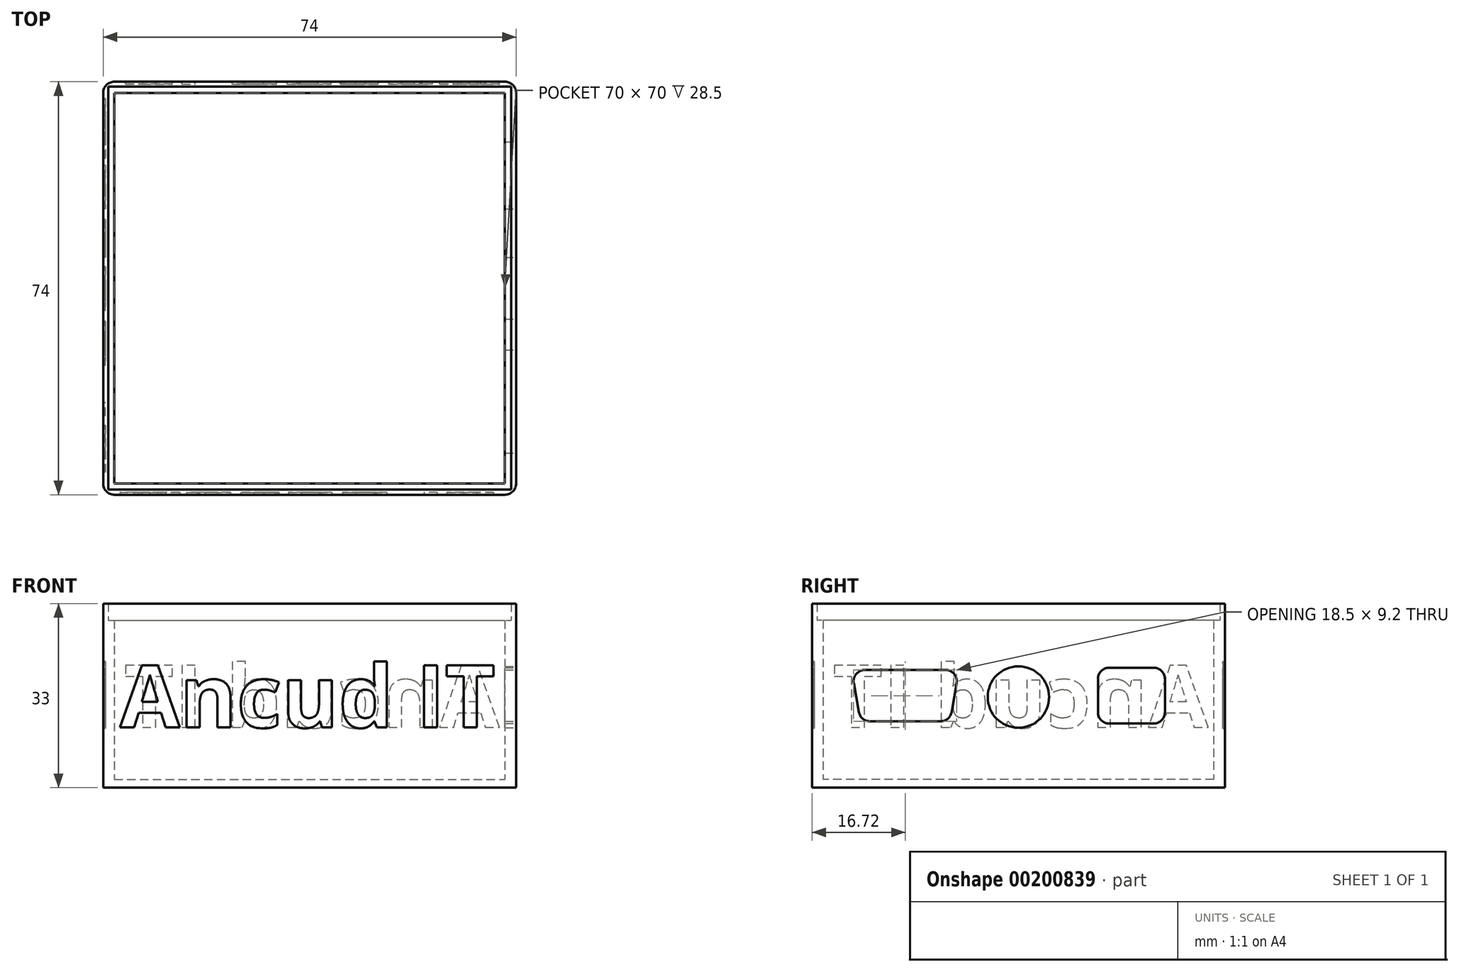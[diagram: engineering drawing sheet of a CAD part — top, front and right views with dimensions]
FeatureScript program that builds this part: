
annotation { "Feature Type Name" : "Feature", "Feature Type Description" : "" }
export const myFeature = defineFeature(function(context is Context, id is Id, definition is map)
    precondition{}
    {
        {
            var Q0;
            Q0=qCreatedBy(makeId("Top.planeOp"),FACE);
            var sketch = newSketch(context, id + "F0", { "sketchPlane" : qUnion([Q0])});
            skLineSegment(sketch, "E0.bottom", {"start": v(-35, 35) * mm, "end": v(35, 35) * mm});
            skLineSegment(sketch, "E0.top", {"start": v(-35, -35) * mm, "end": v(35, -35) * mm});
            skLineSegment(sketch, "E0.left", {"start": v(-35, 35) * mm, "end": v(-35, -35) * mm});
            skLineSegment(sketch, "E0.right", {"start": v(35, 35) * mm, "end": v(35, -35) * mm});
            skLineSegment(sketch, "E1.bottom", {"start": v(-37, 37) * mm, "end": v(37, 37) * mm});
            skLineSegment(sketch, "E1.top", {"start": v(-37, -37) * mm, "end": v(37, -37) * mm});
            skLineSegment(sketch, "E1.left", {"start": v(-37, 37) * mm, "end": v(-37, -37) * mm});
            skLineSegment(sketch, "E1.right", {"start": v(37, 37) * mm, "end": v(37, -37) * mm});
            skSolve(sketch);
        }
        {
            var Q0;
            Q0=makeQuery(id+"F0.imprint","IMPRINT",FACE,{"disambiguationData":[TD([[makeQuery(id+"F0.imprint","IMPRINT",EDGE,{"derivedFrom":sQuery(id+"F0.wireOp",EDGE,"E0.bottom")}),-1.0]])]});
            extrude(context, id + "F1", {"entities" : qUnion([Q0]), "depth" : 1.5 * mm});
        }
        {
            var Q0;
            Q0=makeQuery(id+"F0.imprint","IMPRINT",FACE,{"disambiguationData":[TD([[makeQuery(id+"F0.imprint","IMPRINT",EDGE,{"derivedFrom":sQuery(id+"F0.wireOp",EDGE,"E0.bottom")}),1.0]])]});
            extrude(context, id + "F2", {"entities" : qUnion([Q0]), "operationType" : NewBodyOperationType.ADD, "depth" : 30 * mm});
        }
        {
            var Q0;
            Q0=makeQuery(id+"F2.opExtrude","CAP_FACE",FACE,{"disambiguationData":[OSD([sQuery(id+"F0.wireOp",EDGE,"E0.bottom"),sQuery(id+"F0.wireOp",EDGE,"E0.top"),sQuery(id+"F0.wireOp",EDGE,"E0.left"),sQuery(id+"F0.wireOp",EDGE,"E0.right"),sQuery(id+"F0.wireOp",EDGE,"E1.bottom"),sQuery(id+"F0.wireOp",EDGE,"E1.top"),sQuery(id+"F0.wireOp",EDGE,"E1.left"),sQuery(id+"F0.wireOp",EDGE,"E1.right")])],"isStart":false});
            var sketch = newSketch(context, id + "F3", { "sketchPlane" : qUnion([Q0])});
            skLineSegment(sketch, "E2.bottom", {"start": v(-37, 37) * mm, "end": v(37, 37) * mm});
            skLineSegment(sketch, "E2.top", {"start": v(-37, -37) * mm, "end": v(37, -37) * mm});
            skLineSegment(sketch, "E2.left", {"start": v(-37, 37) * mm, "end": v(-37, -37) * mm});
            skLineSegment(sketch, "E2.right", {"start": v(37, 37) * mm, "end": v(37, -37) * mm});
            skLineSegment(sketch, "E3.bottom", {"start": v(-36.1, 36.1) * mm, "end": v(36.1, 36.1) * mm});
            skLineSegment(sketch, "E3.top", {"start": v(-36.1, -36.1) * mm, "end": v(36.1, -36.1) * mm});
            skLineSegment(sketch, "E3.left", {"start": v(-36.1, 36.1) * mm, "end": v(-36.1, -36.1) * mm});
            skLineSegment(sketch, "E3.right", {"start": v(36.1, 36.1) * mm, "end": v(36.1, -36.1) * mm});
            skSolve(sketch);
        }
        {
            var Q0;
            Q0=makeQuery(id+"F3.imprint","IMPRINT",FACE,{"disambiguationData":[TD([[makeQuery(id+"F3.imprint","IMPRINT",EDGE,{"derivedFrom":sQuery(id+"F3.wireOp",EDGE,"E2.bottom")}),-1.0]])]});
            extrude(context, id + "F4", {"entities" : qUnion([Q0]), "operationType" : NewBodyOperationType.ADD, "depth" : 3 * mm});
        }
        {
            var Q0;
            Q0=makeQuery(id+"F4.boolean.opBoolean","MERGE",FACE,{"derivedFrom":[makeQuery(id+"F2.opExtrude","SWEPT_FACE",FACE,{"disambiguationData":[OSD([sQuery(id+"F0.wireOp",EDGE,"E1.top")])]}),makeQuery(id+"F4.opExtrude","SWEPT_FACE",FACE,{"disambiguationData":[OSD([sQuery(id+"F3.wireOp",EDGE,"E2.top")])]})]});
            var sketch = newSketch(context, id + "F5", { "sketchPlane" : qUnion([Q0])});
            skText(sketch, "E4", { "text": "Ancud IT", "fontName": "OpenSans-Bold.ttf"});
            const initialGuessF5  = {"E4": [-0.034, 0.01079, 1, 0, 0.01121]};
            skSetInitialGuess(sketch, initialGuessF5);
            skSolve(sketch);
        }
        {
            var Q0;
            Q0 = qSketchRegion(id + "F5", true);
            extrude(context, id + "F6", {"entities" : qUnion([Q0]), "operationType" : NewBodyOperationType.REMOVE, "oppositeDirection" : true, "depth" : 0.4 * mm});
        }
        {
            var Q0;
            Q0=makeQuery(id+"F4.boolean.opBoolean","MERGE",FACE,{"derivedFrom":[makeQuery(id+"F2.opExtrude","SWEPT_FACE",FACE,{"disambiguationData":[OSD([sQuery(id+"F0.wireOp",EDGE,"E1.bottom")])]}),makeQuery(id+"F4.opExtrude","SWEPT_FACE",FACE,{"disambiguationData":[OSD([sQuery(id+"F3.wireOp",EDGE,"E2.bottom")])]})]});
            var sketch = newSketch(context, id + "F7", { "sketchPlane" : qUnion([Q0])});
            skText(sketch, "E5", { "text": "Ancud IT", "fontName": "OpenSans-Bold.ttf"});
            const initialGuessF7  = {"E5": [-0.034, 0.01079, 1, 0, 0.01121]};
            skSetInitialGuess(sketch, initialGuessF7);
            skSolve(sketch);
        }
        {
            var Q0;
            Q0 = qSketchRegion(id + "F7", true);
            extrude(context, id + "F8", {"entities" : qUnion([Q0]), "operationType" : NewBodyOperationType.REMOVE, "oppositeDirection" : true, "depth" : 0.4 * mm});
        }
        {
            var Q0;
            Q0=makeQuery(id+"F4.boolean.opBoolean","MERGE",FACE,{"derivedFrom":[makeQuery(id+"F2.opExtrude","SWEPT_FACE",FACE,{"disambiguationData":[OSD([sQuery(id+"F0.wireOp",EDGE,"E1.left")])]}),makeQuery(id+"F4.opExtrude","SWEPT_FACE",FACE,{"disambiguationData":[OSD([sQuery(id+"F3.wireOp",EDGE,"E2.left")])]})]});
            var sketch = newSketch(context, id + "F9", { "sketchPlane" : qUnion([Q0])});
            skText(sketch, "E6", { "text": "Ancud IT", "fontName": "OpenSans-Bold.ttf"});
            const initialGuessF9  = {"E6": [-0.034, 0.01079, 1, 0, 0.01121]};
            skSetInitialGuess(sketch, initialGuessF9);
            skSolve(sketch);
        }
        {
            var Q0;
            Q0 = qSketchRegion(id + "F9", true);
            extrude(context, id + "F10", {"entities" : qUnion([Q0]), "operationType" : NewBodyOperationType.REMOVE, "oppositeDirection" : true, "depth" : 0.4 * mm});
        }
        {
            var Q0;
            Q0=makeQuery(id+"F4.boolean.opBoolean","MERGE",EDGE,{"derivedFrom":[makeQuery(id+"F2.opExtrude","SWEPT_EDGE",EDGE,{"disambiguationData":[OSD([sQuery(id+"F0.wireOp",EDGE,"E1.top"),sQuery(id+"F0.wireOp",EDGE,"E1.right")])]}),makeQuery(id+"F4.opExtrude","SWEPT_EDGE",EDGE,{"disambiguationData":[OSD([sQuery(id+"F3.wireOp",EDGE,"E2.top"),sQuery(id+"F3.wireOp",EDGE,"E2.right")])]})]});
            var Q1;
            Q1=makeQuery(id+"F4.boolean.opBoolean","MERGE",EDGE,{"derivedFrom":[makeQuery(id+"F2.opExtrude","SWEPT_EDGE",EDGE,{"disambiguationData":[OSD([sQuery(id+"F0.wireOp",EDGE,"E1.bottom"),sQuery(id+"F0.wireOp",EDGE,"E1.right")])]}),makeQuery(id+"F4.opExtrude","SWEPT_EDGE",EDGE,{"disambiguationData":[OSD([sQuery(id+"F3.wireOp",EDGE,"E2.bottom"),sQuery(id+"F3.wireOp",EDGE,"E2.right")])]})]});
            var Q2;
            Q2=makeQuery(id+"F4.boolean.opBoolean","MERGE",EDGE,{"derivedFrom":[makeQuery(id+"F2.opExtrude","SWEPT_EDGE",EDGE,{"disambiguationData":[OSD([sQuery(id+"F0.wireOp",EDGE,"E1.bottom"),sQuery(id+"F0.wireOp",EDGE,"E1.left")])]}),makeQuery(id+"F4.opExtrude","SWEPT_EDGE",EDGE,{"disambiguationData":[OSD([sQuery(id+"F3.wireOp",EDGE,"E2.bottom"),sQuery(id+"F3.wireOp",EDGE,"E2.left")])]})]});
            var Q3;
            Q3=makeQuery(id+"F4.boolean.opBoolean","MERGE",EDGE,{"derivedFrom":[makeQuery(id+"F2.opExtrude","SWEPT_EDGE",EDGE,{"disambiguationData":[OSD([sQuery(id+"F0.wireOp",EDGE,"E1.top"),sQuery(id+"F0.wireOp",EDGE,"E1.left")])]}),makeQuery(id+"F4.opExtrude","SWEPT_EDGE",EDGE,{"disambiguationData":[OSD([sQuery(id+"F3.wireOp",EDGE,"E2.top"),sQuery(id+"F3.wireOp",EDGE,"E2.left")])]})]});
            fillet(context, id + "F11", {"entities" : qUnion([Q0, Q1, Q2, Q3]), "radius" : 2 * mm, "tangentPropagation" : true, "allowEdgeOverflow" : false});
        }
        {
            var Q0;
            Q0=makeQuery(id+"F4.boolean.opBoolean","MERGE",FACE,{"derivedFrom":[makeQuery(id+"F2.opExtrude","SWEPT_FACE",FACE,{"disambiguationData":[OSD([sQuery(id+"F0.wireOp",EDGE,"E1.right")])]}),makeQuery(id+"F4.opExtrude","SWEPT_FACE",FACE,{"disambiguationData":[OSD([sQuery(id+"F3.wireOp",EDGE,"E2.right")])]})]});
            var sketch = newSketch(context, id + "F12", { "sketchPlane" : qUnion([Q0])});
            skLineSegment(sketch, "E7", {"start": v(-27.53, 21.1) * mm, "end": v(-13.03, 21.1) * mm});
            skLineSegment(sketch, "E8", {"start": v(-11.06, 18.75) * mm, "end": v(-11.98, 13.55) * mm});
            skLineSegment(sketch, "E9", {"start": v(-13.95, 11.9) * mm, "end": v(-26.61, 11.9) * mm});
            skLineSegment(sketch, "E10", {"start": v(-28.58, 13.55) * mm, "end": v(-29.5, 18.75) * mm});
            skPoint(sketch, "E11.visualSharp", {"position": v(-10.65, 21.1) * mm});
            skArc(sketch, "E11.filletArc", {"start": v(-11.06, 18.75) * mm, "mid": v(-11.5, 20.39) * mm, "end": v(-13.03, 21.1) * mm});
            skPoint(sketch, "E12.visualSharp", {"position": v(-12.27, 11.9) * mm});
            skArc(sketch, "E12.filletArc", {"start": v(-13.95, 11.9) * mm, "mid": v(-12.66, 12.37) * mm, "end": v(-11.98, 13.55) * mm});
            skPoint(sketch, "E13.visualSharp", {"position": v(-28.3, 11.9) * mm});
            skArc(sketch, "E13.filletArc", {"start": v(-28.58, 13.55) * mm, "mid": v(-27.9, 12.37) * mm, "end": v(-26.61, 11.9) * mm});
            skPoint(sketch, "E14.visualSharp", {"position": v(-29.91, 21.1) * mm});
            skArc(sketch, "E14.filletArc", {"start": v(-27.53, 21.1) * mm, "mid": v(-29.06, 20.39) * mm, "end": v(-29.5, 18.75) * mm});
            skCircle(sketch, "E15", {"center": v(0, 16.25) * mm, "radius": 5.5 * mm});
            skLineSegment(sketch, "E16.bottom", {"start": v(14.25, 21.5) * mm, "end": v(26.25, 21.5) * mm});
            skLineSegment(sketch, "E16.top", {"start": v(14.25, 11.5) * mm, "end": v(26.25, 11.5) * mm});
            skLineSegment(sketch, "E16.left", {"start": v(14.25, 21.5) * mm, "end": v(14.25, 11.5) * mm});
            skLineSegment(sketch, "E16.right", {"start": v(26.25, 21.5) * mm, "end": v(26.25, 11.5) * mm});
            skSolve(sketch);
        }
        {
            var Q0;
            Q0=makeQuery(id+"F12.imprint","IMPRINT",FACE,{"disambiguationData":[TD([[makeQuery(id+"F12.imprint","IMPRINT",EDGE,{"derivedFrom":sQuery(id+"F12.wireOp",EDGE,"E7")}),-1.0]])]});
            var Q1;
            Q1=makeQuery(id+"F12.imprint","IMPRINT",FACE,{"disambiguationData":[TD([[makeQuery(id+"F12.imprint","IMPRINT",EDGE,{"derivedFrom":sQuery(id+"F12.wireOp",EDGE,"E15")}),1.0]])]});
            var Q2;
            Q2=makeQuery(id+"F12.imprint","IMPRINT",FACE,{"disambiguationData":[TD([[makeQuery(id+"F12.imprint","IMPRINT",EDGE,{"derivedFrom":sQuery(id+"F12.wireOp",EDGE,"E16.bottom")}),-1.0]])]});
            extrude(context, id + "F13", {"entities" : qUnion([Q0, Q1, Q2]), "operationType" : NewBodyOperationType.REMOVE, "endBound" : BoundingType.UP_TO_NEXT, "oppositeDirection" : true, "depth" : 25 * mm});
        }
        {
            var Q0;
            Q0=makeQuery(id+"F13.boolean.opBoolean","COPY",EDGE,{"derivedFrom":makeQuery(id+"F13.opExtrude","SWEPT_EDGE",EDGE,{"disambiguationData":[OSD([sQuery(id+"F12.wireOp",EDGE,"E16.bottom"),sQuery(id+"F12.wireOp",EDGE,"E16.left")])]})});
            var Q1;
            Q1=makeQuery(id+"F13.boolean.opBoolean","COPY",EDGE,{"derivedFrom":makeQuery(id+"F13.opExtrude","SWEPT_EDGE",EDGE,{"disambiguationData":[OSD([sQuery(id+"F12.wireOp",EDGE,"E16.bottom"),sQuery(id+"F12.wireOp",EDGE,"E16.right")])]})});
            var Q2;
            Q2=makeQuery(id+"F13.boolean.opBoolean","COPY",EDGE,{"derivedFrom":makeQuery(id+"F13.opExtrude","SWEPT_EDGE",EDGE,{"disambiguationData":[OSD([sQuery(id+"F12.wireOp",EDGE,"E16.top"),sQuery(id+"F12.wireOp",EDGE,"E16.left")])]})});
            var Q3;
            Q3=makeQuery(id+"F13.boolean.opBoolean","COPY",EDGE,{"derivedFrom":makeQuery(id+"F13.opExtrude","SWEPT_EDGE",EDGE,{"disambiguationData":[OSD([sQuery(id+"F12.wireOp",EDGE,"E16.top"),sQuery(id+"F12.wireOp",EDGE,"E16.right")])]})});
            fillet(context, id + "F14", {"entities" : qUnion([Q0, Q1, Q2, Q3]), "radius" : 2 * mm, "tangentPropagation" : true, "allowEdgeOverflow" : false});
        }
    });
